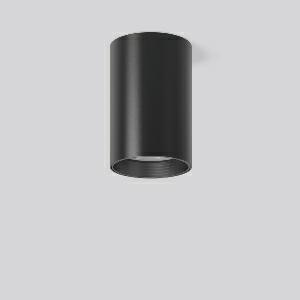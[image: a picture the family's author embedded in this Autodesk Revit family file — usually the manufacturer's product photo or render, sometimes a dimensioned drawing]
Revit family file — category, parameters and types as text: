
# Revit family: heledon_maxi_a_931220_003_1_76_fa0e
name_source: partatom
category: Lighting Fixtures
units: mm (PartAtom-declared; Revit-internal decimal feet)

## family parameters
Cut with Voids When Loaded = No
Host = Face
Light Source = No
Part Type = Normal
Room Calculation Point = No
Round Connector Dimension = Use Diameter
Shared = No

## types (1)
- HELEDON maxi A (1 x LED Modul 940, 3000 lm, 4000)
    Apparent Load = 25 VA
    Approval mark = CE
    CIE Flux Codes = 97 100 100 100 100
    Color Rendering = 92
    Color Temperature = 4000
    Default Elevation = 1800 mm
    Description = Series: HELEDON maxi
Cylindrical surface-mounted downlight. Housing: die-cast aluminium, powder-coated. Internal ceiling frame polycarbonate with bayonet mounting. Black plastic ring and recessed LED to prevent glare from the side. Optical assembly with lens made of plastic (polycarbonate) for the best homogeneous light distribution - can be changed without tools. Best colour rendering index Ra>90. Suitable for Ceiling mounting. Easy installation with a separate ceiling frame with bayonet mounting and plug connection. Driver integrated. Connected via plug-in connector. High quality converter without flickering and stroboscopic effect. The following accessories can be mounted without use of tools: interchangeable lenses, decorative glasses, honeycomb louvre, clear and frosted diffusers, white interchangeable plastic ring. 
Colour: deep black, matt (RAL 9005)
Diameter: 123 mm
Height: 183 mm
Lamp: LED
Socket: without socket
Colour temperature: 4000K
Colour rendering index (CRI): 92
System power: 25 W
Rated luminous flux: 3000 lm
Luminous efficiency: 120 lm/W
Control gear: Converter, dimmable, DALI
Protection class: I
Type of protection: IP 20
    Height = 183 mm
    Lamp = 1 x LED Modul 940
    Lamp Light Flux = 3000 lm
    Lamp count = 1
    Length = 123 mm
    Lifetime = 50000 h
    Luminous efficacy = 120 lm/W
    Manufacturer = RZB
    ModVariant = No
    Model = 931220.003.1.76
    Mounting Place = Ceiling
    Mounting Type = Surface mounted
    Number of Poles = 1
    OnlyDefault = Yes
    Power Factor = 1
    Product Name = HELEDON maxi A
    Product group = Surface mounted downlights
    ProductGroupID = 302
    Protection Class = Protection class I
    Protection Degree = IP 20
    RLX_Detail_Level = 1
    RLX_Emergency_Light_Flux = 0 lm
    RLX_Emergency_Type = 0
    RLX_Emergency_Type_DB = No
    RlxData = <blob elided: 96813 chars, md5=41457ca9>
    Socket = socket
    Standby Power = 0 W
    System Light Flux = 3000 lm
    System Power = 25 W
    Type Comments = Product without accessories
    Type Image = 931193.003.jpg
    URL = http://relux.com
    VarID = ---
    Voltage = 230 V
    Voltage Range = 220-240 V
    Weight = 0.00 kg
    Width = 0 mm  [stored 0 ft]

note: [stored X ft] marks values corroborated as IEEE doubles in the binary element streams (Revit-internal decimal feet)

## geometry (parser evidence)
native form markers: Blend x4, Sweep x10
no freeform markers — native parametric forms only
